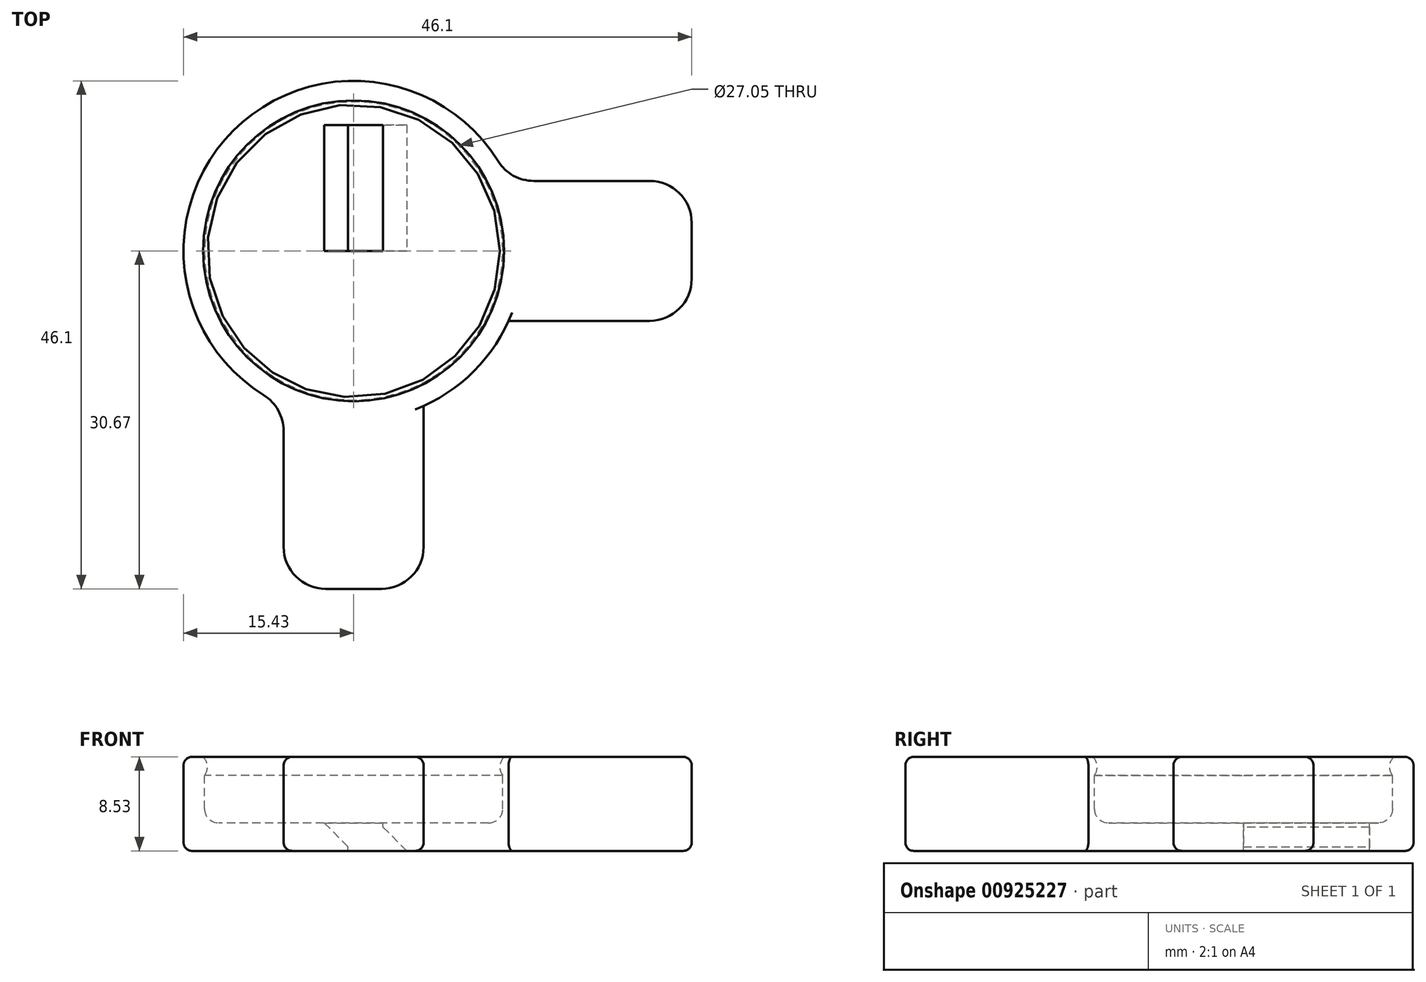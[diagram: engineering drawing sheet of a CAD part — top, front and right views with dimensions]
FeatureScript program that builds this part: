
annotation { "Feature Type Name" : "Feature", "Feature Type Description" : "" }
export const myFeature = defineFeature(function(context is Context, id is Id, definition is map)
    precondition{}
    {
        {
            var Q0;
            Q0=qCreatedBy(makeId("Front.planeOp"),FACE);
            var sketch = newSketch(context, id + "F0", { "sketchPlane" : qUnion([Q0])});
            skLineSegment(sketch, "E0", {"start": v(15.43, 6.71) * mm, "end": v(15.43, 0) * mm});
            skLineSegment(sketch, "E1", {"start": v(15.43, 0) * mm, "end": v(0, 0) * mm});
            skArc(sketch, "E2", {"start": v(15.43, 6.71) * mm, "mid": v(13.63, 6.73) * mm, "end": v(13.65, 8.53) * mm});
            skLineSegment(sketch, "E3", {"start": v(0, 10.9) * mm, "end": v(0, -2.45) * mm, "construction": true});
            skLineSegment(sketch, "E4", {"start": v(0, 0) * mm, "end": v(0, 2.54) * mm});
            skLineSegment(sketch, "E5", {"start": v(0, 2.54) * mm, "end": v(12.26, 2.54) * mm});
            skLineSegment(sketch, "E6", {"start": v(13.53, 3.81) * mm, "end": v(13.53, 6.86) * mm});
            skLineSegment(sketch, "E7", {"start": v(15.43, 6.71) * mm, "end": v(15.43, 8.53) * mm});
            skLineSegment(sketch, "E8", {"start": v(15.43, 8.53) * mm, "end": v(13.65, 8.53) * mm});
            skPoint(sketch, "E9.visualSharp", {"position": v(13.53, 2.54) * mm});
            skArc(sketch, "E10.filletArc", {"start": v(12.26, 2.54) * mm, "mid": v(13.15, 2.91) * mm, "end": v(13.53, 3.81) * mm});
            skPoint(sketch, "E11.visualSharp", {"position": v(15.43, 0) * mm});
            skPoint(sketch, "E12.visualSharp", {"position": v(15.43, 8.53) * mm});
            skSolve(sketch);
        }
        {
            var Q0;
            Q0=qSketchRegion(id+"F0",true);
            var Q1;
            Q1=sQuery(id+"F0.wireOp",EDGE,"E3");
            revolve(context, id + "F1", {"surfaceOperationType" : NewSurfaceOperationType.NEW, "entities" : qUnion([Q0]), "axis" : qUnion([Q1]), "revolveType" : RevolveType.FULL});
        }
        {
            var Q0;
            Q0=makeQuery(id+"F1.opRevolve","SWEPT_FACE",FACE,{"disambiguationData":[OSD([sQuery(id+"F0.wireOp",EDGE,"E8")])]});
            var sketch = newSketch(context, id + "F2", { "sketchPlane" : qUnion([Q0])});
            skLineSegment(sketch, "E13.bottom", {"start": v(30.67, 6.35) * mm, "end": v(14.06, 6.35) * mm});
            skLineSegment(sketch, "E13.top", {"start": v(30.67, -6.35) * mm, "end": v(14.06, -6.35) * mm});
            skLineSegment(sketch, "E13.left", {"start": v(30.67, 6.35) * mm, "end": v(30.67, -6.35) * mm});
            skLineSegment(sketch, "E14.bottom", {"start": v(6.35, -30.67) * mm, "end": v(-6.35, -30.67) * mm});
            skLineSegment(sketch, "E14.left", {"start": v(6.35, -30.67) * mm, "end": v(6.35, -14.06) * mm});
            skLineSegment(sketch, "E14.right", {"start": v(-6.35, -30.67) * mm, "end": v(-6.35, -14.06) * mm});
            skArc(sketch, "E15.0", {"start": v(-6.35, -14.06) * mm, "mid": v(0, -15.43) * mm, "end": v(6.35, -14.06) * mm});
            skArc(sketch, "E16.trimOffspring", {"start": v(14.06, -6.35) * mm, "mid": v(15.43, 0) * mm, "end": v(14.06, 6.35) * mm});
            skSolve(sketch);
        }
        {
            var Q0;
            Q0=qSketchRegion(id+"F2",true);
            var Q1;
            Q1=makeQuery(id+"F1.opRevolve","SWEPT_FACE",FACE,{"disambiguationData":[OSD([sQuery(id+"F0.wireOp",EDGE,"E1")])]});
            extrude(context, id + "F3", {"entities" : qUnion([Q0]), "operationType" : NewBodyOperationType.ADD, "endBound" : BoundingType.UP_TO_SURFACE, "oppositeDirection" : true, "depth" : 25.4 * mm, "endBoundEntityFace" : qUnion([Q1]), "offsetDistance" : 25.4 * mm});
        }
        {
            var Q0;
            Q0=makeQuery(id+"F3.opExtrude","SWEPT_EDGE",EDGE,{"disambiguationData":[OSD([sQuery(id+"F2.wireOp",EDGE,"E14.bottom"),sQuery(id+"F2.wireOp",EDGE,"E14.right")])]});
            var Q1;
            Q1=makeQuery(id+"F3.opExtrude","SWEPT_EDGE",EDGE,{"disambiguationData":[OSD([sQuery(id+"F0.wireOp",EDGE,"E7"),sQuery(id+"F0.wireOp",EDGE,"E8"),sQuery(id+"F2.wireOp",EDGE,"E14.right"),sQuery(id+"F2.wireOp",EDGE,"E15.0")])]});
            var Q2;
            Q2=makeQuery(id+"F3.opExtrude","SWEPT_EDGE",EDGE,{"disambiguationData":[OSD([sQuery(id+"F2.wireOp",EDGE,"E14.bottom"),sQuery(id+"F2.wireOp",EDGE,"E14.left")])]});
            var Q3;
            Q3=makeQuery(id+"F3.opExtrude","SWEPT_EDGE",EDGE,{"disambiguationData":[OSD([sQuery(id+"F0.wireOp",EDGE,"E7"),sQuery(id+"F0.wireOp",EDGE,"E8"),sQuery(id+"F2.wireOp",EDGE,"E14.left"),sQuery(id+"F2.wireOp",EDGE,"E15.0")])]});
            var Q4;
            Q4=makeQuery(id+"F3.opExtrude","SWEPT_EDGE",EDGE,{"disambiguationData":[OSD([sQuery(id+"F0.wireOp",EDGE,"E7"),sQuery(id+"F0.wireOp",EDGE,"E8"),sQuery(id+"F2.wireOp",EDGE,"E13.top"),sQuery(id+"F2.wireOp",EDGE,"E16.trimOffspring")])]});
            var Q5;
            Q5=makeQuery(id+"F3.opExtrude","SWEPT_EDGE",EDGE,{"disambiguationData":[OSD([sQuery(id+"F2.wireOp",EDGE,"E13.top"),sQuery(id+"F2.wireOp",EDGE,"E13.left")])]});
            var Q6;
            Q6=makeQuery(id+"F3.opExtrude","SWEPT_EDGE",EDGE,{"disambiguationData":[OSD([sQuery(id+"F2.wireOp",EDGE,"E13.bottom"),sQuery(id+"F2.wireOp",EDGE,"E13.left")])]});
            var Q7;
            Q7=makeQuery(id+"F3.opExtrude","SWEPT_EDGE",EDGE,{"disambiguationData":[OSD([sQuery(id+"F0.wireOp",EDGE,"E7"),sQuery(id+"F0.wireOp",EDGE,"E8"),sQuery(id+"F2.wireOp",EDGE,"E13.bottom"),sQuery(id+"F2.wireOp",EDGE,"E16.trimOffspring")])]});
            fillet(context, id + "F4", {"entities" : qUnion([Q0, Q1, Q2, Q3, Q4, Q5, Q6, Q7]), "radius" : 3.8 * mm, "tangentPropagation" : true, "allowEdgeOverflow" : false});
        }
        {
            var Q0;
            Q0=makeQuery(id+"F3.opExtrude","CAP_EDGE",EDGE,{"disambiguationData":[OSD([sQuery(id+"F2.wireOp",EDGE,"E14.bottom")])],"isStart":true});
            var Q1;
            Q1=makeQuery(id+"F3.opExtrude","CAP_EDGE",EDGE,{"disambiguationData":[OSD([sQuery(id+"F2.wireOp",EDGE,"E14.bottom")])],"isStart":false});
            fillet(context, id + "F5", {"entities" : qUnion([Q0, Q1]), "radius" : 0.76 * mm, "tangentPropagation" : true, "allowEdgeOverflow" : false});
        }
        {
            var Q0;
            Q0=makeQuery(id+"F1.opRevolve","SWEPT_FACE",FACE,{"disambiguationData":[OSD([sQuery(id+"F0.wireOp",EDGE,"E5")])]});
            var sketch = newSketch(context, id + "F6", { "sketchPlane" : qUnion([Q0])});
            skSolve(sketch);
        }
        {
            var Q0;
            Q0=makeQuery(id+"F6.imprint","IMPRINT",FACE,{"disambiguationData":[TD([[makeQuery(id+"F6.imprint","IMPRINT",EDGE,{"derivedFrom":makeQuery(id+"F1.opRevolve","SWEPT_EDGE",EDGE,{"disambiguationData":[OSD([sQuery(id+"F0.wireOp",EDGE,"E5"),sQuery(id+"F0.wireOp",EDGE,"E10.filletArc")])]})}),1.0]])]});
            var sketch = newSketch(context, id + "F7", { "sketchPlane" : qUnion([Q0])});
            skLineSegment(sketch, "E17", {"start": v(-0.5, 0) * mm, "end": v(-0.5, 11.43) * mm});
            skLineSegment(sketch, "E18", {"start": v(-0.5, 11.43) * mm, "end": v(2.67, 11.43) * mm});
            skLineSegment(sketch, "E19", {"start": v(2.67, 11.43) * mm, "end": v(2.67, 0) * mm});
            skLineSegment(sketch, "E20", {"start": v(2.67, 0) * mm, "end": v(-0.5, 0) * mm});
            skSolve(sketch);
        }
        {
            var Q0;
            Q0 = qSketchRegion(id + "F7", true);
            extrude(context, id + "F8", {"entities" : qUnion([Q0]), "operationType" : NewBodyOperationType.REMOVE, "oppositeDirection" : true, "depth" : 25.4 * mm, "offsetDistance" : 25.4 * mm});
        }
        {
            var Q0;
            Q0=makeQuery(id+"F8.boolean.opBoolean","COPY",FACE,{"derivedFrom":makeQuery(id+"F8.opExtrude","SWEPT_FACE",FACE,{"disambiguationData":[OSD([sQuery(id+"F7.wireOp",EDGE,"E20")])]})});
            var sketch = newSketch(context, id + "F9", { "sketchPlane" : qUnion([Q0])});
            skLineSegment(sketch, "E21", {"start": v(2.67, 2.54) * mm, "end": v(2.67, 2.54) * mm});
            skPoint(sketch, "E22.end.orphan", {"position": v(-2.67, 0) * mm});
            skLineSegment(sketch, "E23", {"start": v(-4.83, 0) * mm, "end": v(-2.67, 2.16) * mm});
            skLineSegment(sketch, "E24", {"start": v(-2.67, 2.54) * mm, "end": v(-3.84, 2.54) * mm, "construction": true});
            skLineSegment(sketch, "E25", {"start": v(-2.67, 0) * mm, "end": v(-4.83, 0) * mm});
            skLineSegment(sketch, "E26", {"start": v(-2.67, 2.16) * mm, "end": v(-2.67, 0) * mm});
            skLineSegment(sketch, "E27", {"start": v(2.67, 2.54) * mm, "end": v(0.13, 0) * mm});
            skLineSegment(sketch, "E28", {"start": v(2.67, 2.54) * mm, "end": v(0.1, 2.54) * mm});
            skLineSegment(sketch, "E29", {"start": v(0.1, 2.54) * mm, "end": v(0.13, 0) * mm});
            skLineSegment(sketch, "E30", {"start": v(0, 0) * mm, "end": v(1.65, 0) * mm, "construction": true});
            skSolve(sketch);
        }
        {
            var Q0;
            Q0 = qSketchRegion(id + "F9", true);
            var Q1;
            Q1=makeQuery(id+"F8.boolean.opBoolean","COPY",FACE,{"derivedFrom":makeQuery(id+"F8.opExtrude","SWEPT_FACE",FACE,{"disambiguationData":[OSD([sQuery(id+"F7.wireOp",EDGE,"E18")])]})});
            extrude(context, id + "F10", {"entities" : qUnion([Q0]), "operationType" : NewBodyOperationType.REMOVE, "endBound" : BoundingType.UP_TO_SURFACE, "depth" : 25.4 * mm, "endBoundEntityFace" : qUnion([Q1]), "offsetDistance" : 25.4 * mm});
        }
    });
